# Revit family: 434360001_Ducha Nogal Redonda 8 Pulgadas
name_source: partatom
category: Plumbing Fixtures
units: mm (PartAtom-declared; Revit-internal decimal feet)

## family parameters
Always vertical = Yes
Cut with Voids When Loaded = No
Host = Wall
OmniClass Number = 23.31.17.00
OmniClass Title = Showers
Part Type = Normal
Room Calculation Point = No
Round Connector Dimension = Use Diameter
Shared = No

## types (1)
- Type 1
    Alto Ducha = 129 mm
    Alto Llave = 69 mm
    Altura Ducha = 1800 mm
    Altura Llave = 900 mm  [stored 2.95276 ft]
    Ancho Ducha = 117 mm
    Ancho Llave = 332 mm  [stored 1.08924 ft]
    Capacidad de flujo = 9,5 L/min.
    Creado por = BIMBAU
    Default Elevation = 0 mm  [stored 0 ft]
    Description = La línea Nogal es la solución para cualquier sistema de instalación con diferentes productos bajo un mismo concepto de diseño.
    Fecha de creación = 09/04/2021
    Garantía = 30 Años Grival - 5 Años Cromado
    Manufacturer = Grival
    Material = Corona_Aluminio
    Material 2 = Corona_Plastico_Gris
    Model = Ducha Nogal 8 Pulgadas Cosmos Redonda SSB
    Peso Bruto aprox = 1070gr. / 2,36Lb.
    Peso Neto aprox = 955gr. / 2,11Lb.
    Presion maxima = 125 psi.
    Presion minima = 20 psi.
    Profundidad Ducha = 235 mm
    Referencia = 434360001
    Temperaturas máxima de trabajo = 71 ºC / 159,8 ºF.
    Temperaturas mínima de trabajo = 5 ºC / 41 ºF.
    URL = https://bimbau.s3.amazonaws.com
    Vida útil = 10.000 ciclos.

note: [stored X ft] marks values corroborated as IEEE doubles in the binary element streams (Revit-internal decimal feet)

## geometry (parser evidence)
native form markers: Sweep x5
no freeform markers — native parametric forms only
